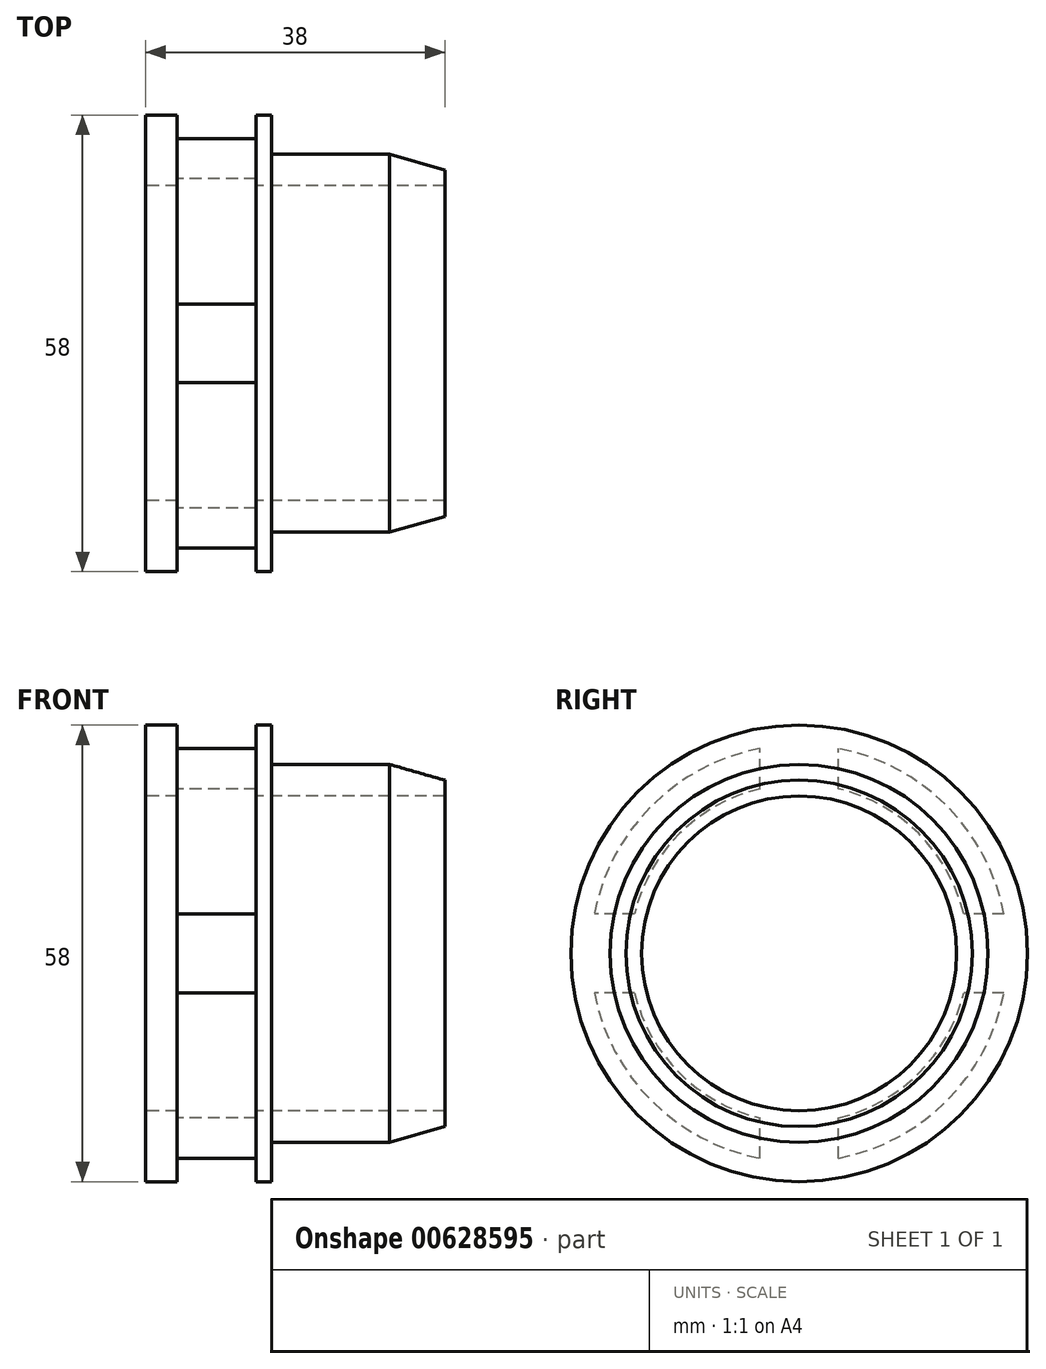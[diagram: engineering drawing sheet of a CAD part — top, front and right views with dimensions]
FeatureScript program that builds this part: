
annotation { "Feature Type Name" : "Feature", "Feature Type Description" : "" }
export const myFeature = defineFeature(function(context is Context, id is Id, definition is map)
    precondition{}
    {
        {
            var Q0;
            Q0=qCreatedBy(makeId("Front.planeOp"),FACE);
            var sketch = newSketch(context, id + "F0", { "sketchPlane" : qUnion([Q0])});
            skLineSegment(sketch, "E0", {"start": v(0, 20) * mm, "end": v(0, 29) * mm});
            skLineSegment(sketch, "E1", {"start": v(0, 29) * mm, "end": v(4, 29) * mm});
            skLineSegment(sketch, "E2", {"start": v(4, 29) * mm, "end": v(4, 26.5) * mm});
            skLineSegment(sketch, "E3", {"start": v(4, 26.5) * mm, "end": v(14, 26.5) * mm});
            skLineSegment(sketch, "E4", {"start": v(14, 26.5) * mm, "end": v(14, 29) * mm});
            skLineSegment(sketch, "E5", {"start": v(14, 29) * mm, "end": v(16, 29) * mm});
            skLineSegment(sketch, "E6", {"start": v(16, 29) * mm, "end": v(16, 24) * mm});
            skLineSegment(sketch, "E7", {"start": v(16, 24) * mm, "end": v(31, 24) * mm});
            skLineSegment(sketch, "E8", {"start": v(31, 24) * mm, "end": v(38, 22) * mm});
            skLineSegment(sketch, "E9", {"start": v(38, 22) * mm, "end": v(38, 20) * mm});
            skLineSegment(sketch, "E10", {"start": v(38, 0) * mm, "end": v(0, 0) * mm});
            skLineSegment(sketch, "E11", {"start": v(0, 0) * mm, "end": v(73.73, 0) * mm, "construction": true});
            skLineSegment(sketch, "E12", {"start": v(0, 20) * mm, "end": v(4, 20) * mm});
            skLineSegment(sketch, "E13", {"start": v(4, 21.5) * mm, "end": v(14, 21.5) * mm});
            skLineSegment(sketch, "E14", {"start": v(4, 21.5) * mm, "end": v(4, 20) * mm});
            skLineSegment(sketch, "E15", {"start": v(14, 21.5) * mm, "end": v(14, 20) * mm});
            skLineSegment(sketch, "E16.trimOffspring", {"start": v(14, 20) * mm, "end": v(38, 20) * mm});
            skSolve(sketch);
        }
        {
            var Q0;
            Q0 = qSketchRegion(id + "F0", true);
            var Q1;
            Q1=sQuery(id+"F0.wireOp",EDGE,"E11");
            revolve(context, id + "F1", {"surfaceOperationType" : NewSurfaceOperationType.NEW, "entities" : qUnion([Q0]), "axis" : qUnion([Q1]), "revolveType" : RevolveType.FULL});
        }
        {
            var Q0;
            Q0=qCreatedBy(makeId("Front.planeOp"),FACE);
            var sketch = newSketch(context, id + "F2", { "sketchPlane" : qUnion([Q0])});
            skLineSegment(sketch, "E17.bottom", {"start": v(4, 5) * mm, "end": v(14, 5) * mm});
            skLineSegment(sketch, "E17.top", {"start": v(4, -5) * mm, "end": v(14, -5) * mm});
            skLineSegment(sketch, "E17.left", {"start": v(4, 5) * mm, "end": v(4, -5) * mm});
            skLineSegment(sketch, "E17.right", {"start": v(14, 5) * mm, "end": v(14, -5) * mm});
            skSolve(sketch);
        }
        {
            var Q0;
            Q0 = qSketchRegion(id + "F2", true);
            extrude(context, id + "F3", {"entities" : qUnion([Q0]), "operationType" : NewBodyOperationType.REMOVE, "oppositeDirection" : true, "depth" : 100 * mm, "offsetDistance" : 25 * mm, "hasSecondDirection" : true, "secondDirectionOppositeDirection" : false, "secondDirectionDepth" : 100 * mm});
        }
        {
            var Q0;
            Q0=qCreatedBy(makeId("Top.planeOp"),FACE);
            var sketch = newSketch(context, id + "F4", { "sketchPlane" : qUnion([Q0])});
            skLineSegment(sketch, "E18.bottom", {"start": v(4, 5) * mm, "end": v(14, 5) * mm});
            skLineSegment(sketch, "E18.top", {"start": v(4, -5) * mm, "end": v(14, -5) * mm});
            skLineSegment(sketch, "E18.left", {"start": v(4, 5) * mm, "end": v(4, -5) * mm});
            skLineSegment(sketch, "E18.right", {"start": v(14, 5) * mm, "end": v(14, -5) * mm});
            skSolve(sketch);
        }
        {
            var Q0;
            Q0 = qSketchRegion(id + "F4", true);
            extrude(context, id + "F5", {"entities" : qUnion([Q0]), "operationType" : NewBodyOperationType.REMOVE, "oppositeDirection" : true, "depth" : 50 * mm, "offsetDistance" : 25 * mm, "hasSecondDirection" : true, "secondDirectionOppositeDirection" : false, "secondDirectionDepth" : 50 * mm});
        }
    });
